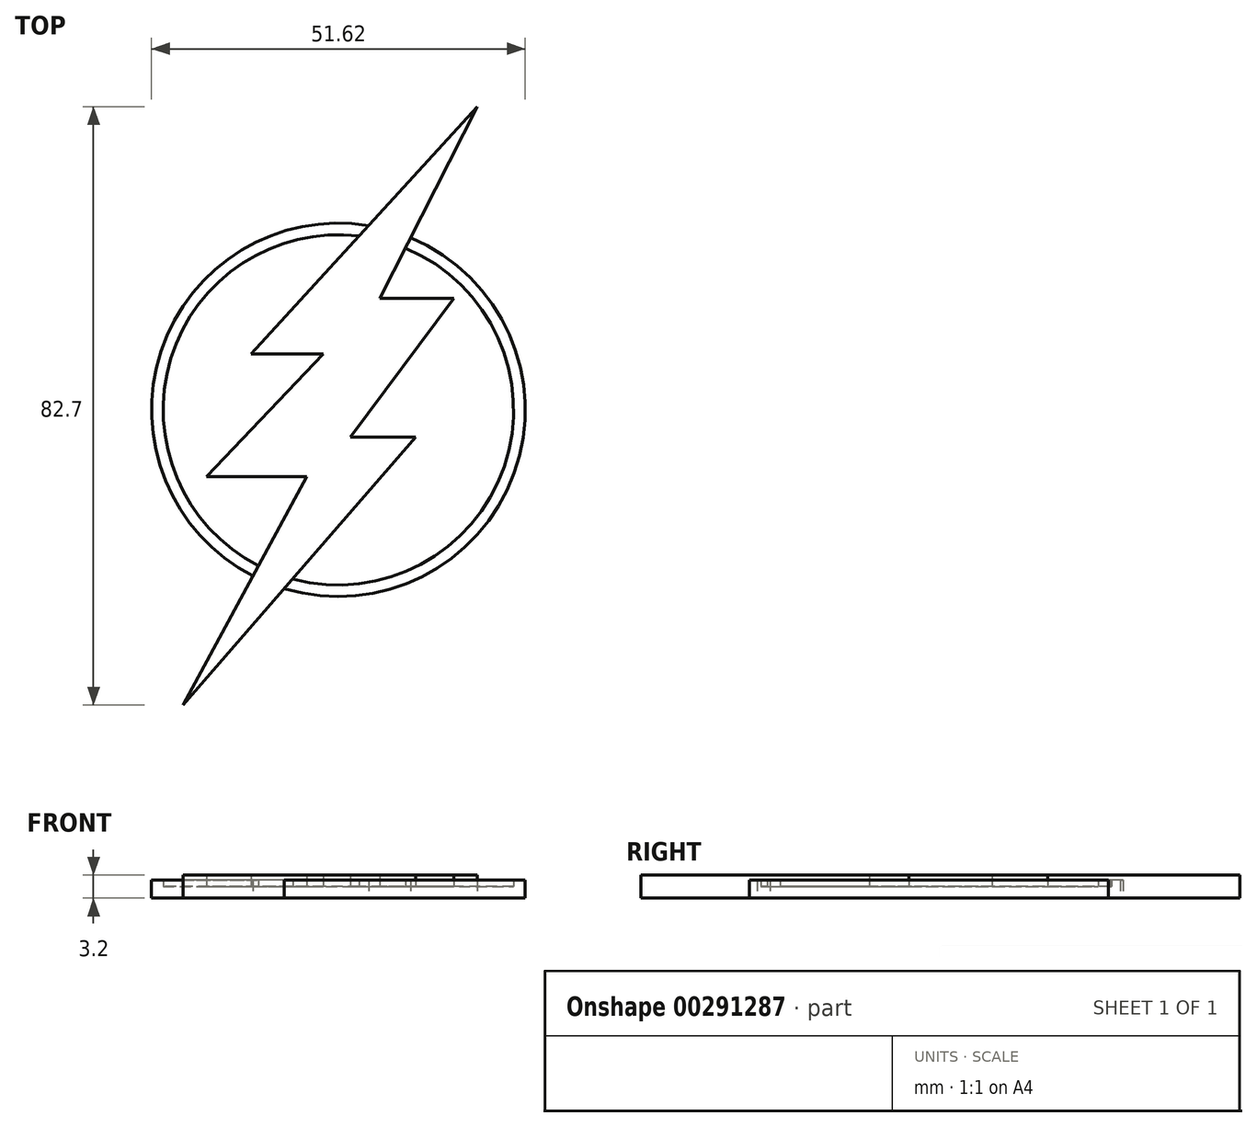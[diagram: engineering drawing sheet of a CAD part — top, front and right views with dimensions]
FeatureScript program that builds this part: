
annotation { "Feature Type Name" : "Feature", "Feature Type Description" : "" }
export const myFeature = defineFeature(function(context is Context, id is Id, definition is map)
    precondition{}
    {
        {
            var Q0;
            Q0=qCreatedBy(makeId("Top.planeOp"),FACE);
            var sketch = newSketch(context, id + "F0", { "sketchPlane" : qUnion([Q0])});
            skCircle(sketch, "E0", {"center": v(0, 0) * mm, "radius": 24.2 * mm});
            skLineSegment(sketch, "E1", {"start": v(19.2, 41.92) * mm, "end": v(-12.03, 7.7) * mm});
            skLineSegment(sketch, "E2", {"start": v(-12.03, 7.7) * mm, "end": v(-2.07, 7.7) * mm});
            skLineSegment(sketch, "E3", {"start": v(-2.07, 7.7) * mm, "end": v(-18.23, -9.2) * mm});
            skLineSegment(sketch, "E4", {"start": v(-18.23, -9.2) * mm, "end": v(-4.37, -9.2) * mm});
            skLineSegment(sketch, "E5", {"start": v(-4.37, -9.2) * mm, "end": v(-21.43, -40.78) * mm});
            skLineSegment(sketch, "E6", {"start": v(-21.43, -40.78) * mm, "end": v(10.7, -3.76) * mm});
            skLineSegment(sketch, "E7", {"start": v(10.7, -3.76) * mm, "end": v(1.67, -3.76) * mm});
            skLineSegment(sketch, "E8", {"start": v(1.67, -3.76) * mm, "end": v(15.98, 15.41) * mm});
            skLineSegment(sketch, "E9", {"start": v(15.98, 15.41) * mm, "end": v(5.73, 15.41) * mm});
            skLineSegment(sketch, "E10", {"start": v(5.73, 15.41) * mm, "end": v(19.2, 41.92) * mm});
            skCircle(sketch, "E11", {"center": v(0, 0) * mm, "radius": 25.8 * mm});
            skSolve(sketch);
        }
        {
            var Q0;
            Q0=makeQuery(id+"F0.imprint","IMPRINT",FACE,{"disambiguationData":[TD([[makeQuery(id+"F0.imprint","IMPRINT",EDGE,{"derivedFrom":sQuery(id+"F0.wireOp",EDGE,"E0")}),1.0]])]});
            var Q1;
            {var subQ0=sQuery(id+"F0.wireOp",EDGE,"E5");var subQ1=sQuery(id+"F0.wireOp",EDGE,"E0");var subQ2=makeQuery(id+"F0.imprint","INTERSECT",VERTEX,{"derivedFrom":[subQ1,subQ0]});Q1=makeQuery(id+"F0.imprint","IMPRINT",FACE,{"disambiguationData":[TD([[makeQuery(id+"F0.imprint","IMPRINT",EDGE,{"disambiguationData":[TD([[subQ2,-1.0]])],"derivedFrom":subQ1}),-1.0]])]});}
            var Q2;
            {var subQ0=sQuery(id+"F0.wireOp",EDGE,"E1");var subQ1=sQuery(id+"F0.wireOp",EDGE,"E0");var subQ2=makeQuery(id+"F0.imprint","INTERSECT",VERTEX,{"derivedFrom":[subQ1,subQ0]});Q2=makeQuery(id+"F0.imprint","IMPRINT",FACE,{"disambiguationData":[TD([[makeQuery(id+"F0.imprint","IMPRINT",EDGE,{"disambiguationData":[TD([[subQ2,1.0]])],"derivedFrom":subQ1}),-1.0]])]});}
            var Q3;
            {var subQ0=sQuery(id+"F0.wireOp",EDGE,"E10");var subQ1=sQuery(id+"F0.wireOp",EDGE,"E1");var subQ2=makeQuery(id+"F0.imprint","INTERSECT",VERTEX,{"derivedFrom":[subQ1,subQ0]});Q3=makeQuery(id+"F0.imprint","IMPRINT",FACE,{"disambiguationData":[TD([[makeQuery(id+"F0.imprint","IMPRINT",EDGE,{"disambiguationData":[TD([[subQ2,-1.0]])],"derivedFrom":subQ1}),1.0]])]});}
            var Q4;
            {var subQ0=sQuery(id+"F0.wireOp",EDGE,"E6");var subQ1=sQuery(id+"F0.wireOp",EDGE,"E5");var subQ2=makeQuery(id+"F0.imprint","INTERSECT",VERTEX,{"derivedFrom":[subQ1,subQ0]});Q4=makeQuery(id+"F0.imprint","IMPRINT",FACE,{"disambiguationData":[TD([[makeQuery(id+"F0.imprint","IMPRINT",EDGE,{"disambiguationData":[TD([[subQ2,1.0]])],"derivedFrom":subQ1}),1.0]])]});}
            extrude(context, id + "F1", {"entities" : qUnion([Q0, Q1, Q2, Q3, Q4]), "depth" : 3.2 * mm});
        }
        {
            var Q0;
            {var subQ5=sQuery(id+"F0.wireOp",EDGE,"E7");Q0=makeQuery(id+"F0.imprint","IMPRINT",FACE,{"disambiguationData":[TD([[makeQuery(id+"F0.imprint","IMPRINT",EDGE,{"derivedFrom":subQ5}),-1.0]])]});}
            var Q1;
            {var subQ0=sQuery(id+"F0.wireOp",EDGE,"E2");Q1=makeQuery(id+"F0.imprint","IMPRINT",FACE,{"disambiguationData":[TD([[makeQuery(id+"F0.imprint","IMPRINT",EDGE,{"derivedFrom":subQ0}),-1.0]])]});}
            extrude(context, id + "F2", {"entities" : qUnion([Q0, Q1]), "operationType" : NewBodyOperationType.ADD, "depth" : 1.6 * mm});
        }
        {
            var Q0;
            {var subQ0=sQuery(id+"F0.wireOp",EDGE,"E1");var subQ1=sQuery(id+"F0.wireOp",EDGE,"E0");var subQ2=makeQuery(id+"F0.imprint","INTERSECT",VERTEX,{"derivedFrom":[subQ1,subQ0]});Q0=makeQuery(id+"F0.imprint","IMPRINT",FACE,{"disambiguationData":[TD([[makeQuery(id+"F0.imprint","IMPRINT",EDGE,{"disambiguationData":[TD([[subQ2,-1.0]])],"derivedFrom":subQ1}),-1.0]])]});}
            var Q1;
            {var subQ0=sQuery(id+"F0.wireOp",EDGE,"E10");var subQ1=sQuery(id+"F0.wireOp",EDGE,"E0");var subQ2=makeQuery(id+"F0.imprint","INTERSECT",VERTEX,{"derivedFrom":[subQ1,subQ0]});Q1=makeQuery(id+"F0.imprint","IMPRINT",FACE,{"disambiguationData":[TD([[makeQuery(id+"F0.imprint","IMPRINT",EDGE,{"disambiguationData":[TD([[subQ2,1.0]])],"derivedFrom":subQ1}),-1.0]])]});}
            extrude(context, id + "F3", {"entities" : qUnion([Q0, Q1]), "operationType" : NewBodyOperationType.ADD, "depth" : 2.5 * mm});
        }
    });
